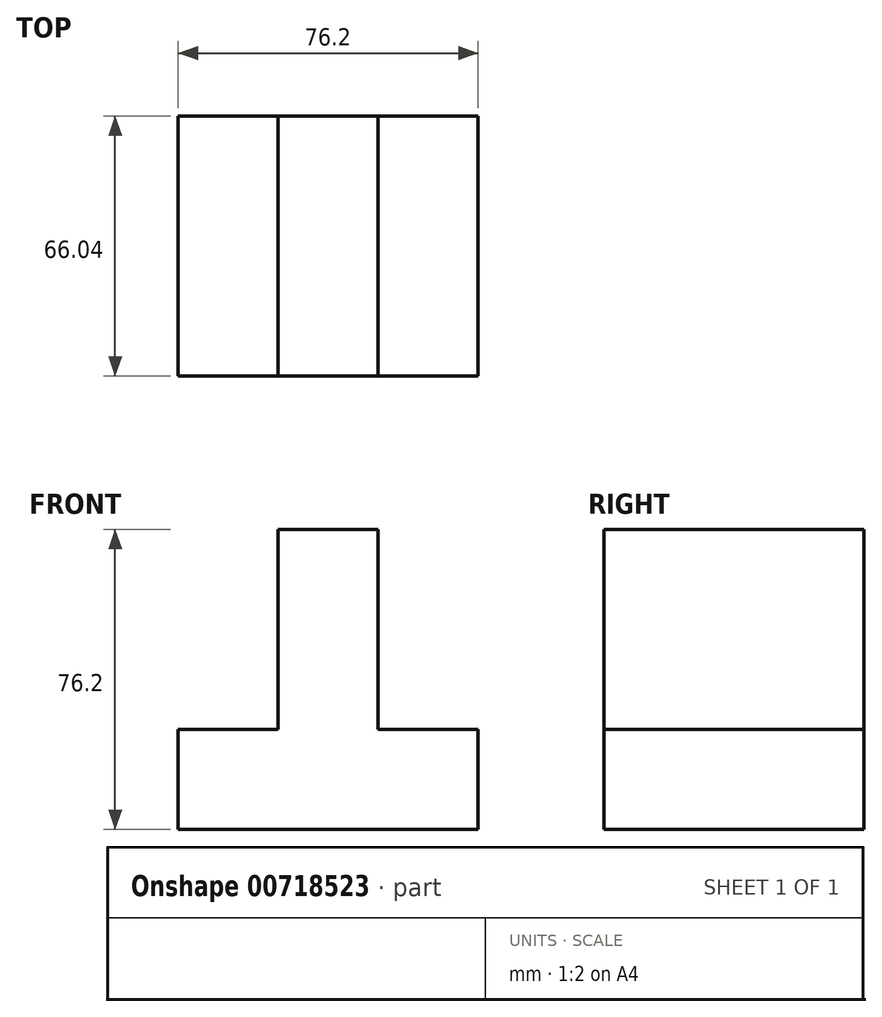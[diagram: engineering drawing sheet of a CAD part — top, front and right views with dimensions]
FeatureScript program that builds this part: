
annotation { "Feature Type Name" : "Feature", "Feature Type Description" : "" }
export const myFeature = defineFeature(function(context is Context, id is Id, definition is map)
    precondition{}
    {
        {
            var Q0;
            Q0=qCreatedBy(makeId("Front.planeOp"),FACE);
            var sketch = newSketch(context, id + "F0", { "sketchPlane" : qUnion([Q0])});
            skLineSegment(sketch, "E0", {"start": v(14.2, 47) * mm, "end": v(-11.2, 47) * mm});
            skLineSegment(sketch, "E1", {"start": v(-11.2, 47) * mm, "end": v(-11.2, -3.8) * mm});
            skLineSegment(sketch, "E2", {"start": v(-11.2, -3.8) * mm, "end": v(-36.6, -3.8) * mm});
            skLineSegment(sketch, "E3", {"start": v(-36.6, -3.8) * mm, "end": v(-36.6, -29.2) * mm});
            skLineSegment(sketch, "E4", {"start": v(-36.6, -29.2) * mm, "end": v(39.6, -29.2) * mm});
            skLineSegment(sketch, "E5", {"start": v(39.6, -29.2) * mm, "end": v(39.6, -3.8) * mm});
            skLineSegment(sketch, "E6", {"start": v(39.6, -3.8) * mm, "end": v(14.2, -3.8) * mm});
            skLineSegment(sketch, "E7", {"start": v(14.2, -3.8) * mm, "end": v(14.2, 47) * mm});
            skSolve(sketch);
        }
        {
            var Q0;
            Q0 = qSketchRegion(id + "F0", true);
            extrude(context, id + "F1", {"entities" : qUnion([Q0]), "depth" : 66.04 * mm, "offsetDistance" : 25.4 * mm});
        }
    });
